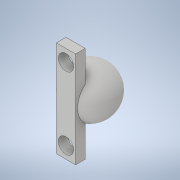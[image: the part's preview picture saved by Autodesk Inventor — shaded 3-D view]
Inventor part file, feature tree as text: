
AUTODESK INVENTOR PART (.ipt)
format: ipt  version: 2020 (Build 240168000, 168)  size: 141,312 bytes
history: native  units: mm
features: sketch x4, other x1, revolve x1, plane x1, extrude x1, hole x1
ambient origin geometry x8: Origin, YZ Plane, XZ Plane, XY Plane, X Axis, Y Axis, Z Axis, Center Point
bodies: Body1 (feature_tree)
feature tree (9):
  other  "Sólido1"
  revolve  "Revolución1"  [1 undecoded]
  plane  "Plano de trabajo1"
  extrude  "Extrusión1"  Depth=20.0mm
  hole  "Agujero1"  [1 undecoded]
  sketch  "Sketch4"  dims[d7=3.175mm d8=6.0mm d9=4.0mm d10=2.0mm d11=90.0deg d12=8.0mm d13=20.594885mm]
  sketch  "Boceto1"  dims[d1=90.0deg d2=5.0mm]
  sketch  "Boceto2"  dims[d3=4.0mm d4=20.0mm]
  sketch  "Boceto3"  dims[d5=2.0mm d6=0.0mm]
note: 2 required parameter values undecoded (feature->parameter linkage not recoverable at this tier; creation-order binding heuristic only, values carry confidence <= 0.55)